# Revit family: Proto Low Chair IN
name_source: partatom
category: Furniture
revit_build: Autodesk Revit 2017 (Build: 20171027_0315(x64)
units: mm (PartAtom-declared; Revit-internal decimal feet)

## family parameters
Always vertical = Yes
Cut with Voids When Loaded = No
OmniClass Number = 23.40.20.00
OmniClass Title = General Furniture and Specialties
Room Calculation Point = No
Shared = No
Work Plane-Based = No

## types (1)
- Proto Low Chair IN
    Backrest modify = Change Backrest Upholstery in Manage -> Object Styles ->Imported Objects
    Base = +Halle Steelcut Trio 3 - 0796
    DS/EN Strength, durability and safety = EN1022:2005 L2: Extreme Use
    Depth (cm) = 74
    Depth (in) = 29,1
    EN Strength, durability and safety = EN16139:2013 L2: Extreme Use
    Flame resistance BS = Foam BS5852 crib 5 certified (US does not apply)
    Gliders = +Halle PP - white
    Height (cm) = 81
    Height (in) = 31,9
    Packaging Dimensions (cm) = 80 / 93 / 87
    Packaging Dimensions (in) = 176.4 / 205.1 / 191.8
    Product family = Proto
    Seating Height (cm) = 45
    Seating Height (in) = 17,7
    URL = https://www.plushalle.com
    Variations = All standard fabrics can be recommended
    Warranty period = 2 years standard warranty
    Weight (kg) = 32
    Weight (lbs) = 70,5
    Width (cm) = 87
    Width (in) = 34,3

## geometry (parser evidence)
native form markers: Sweep x2
no freeform markers — native parametric forms only
